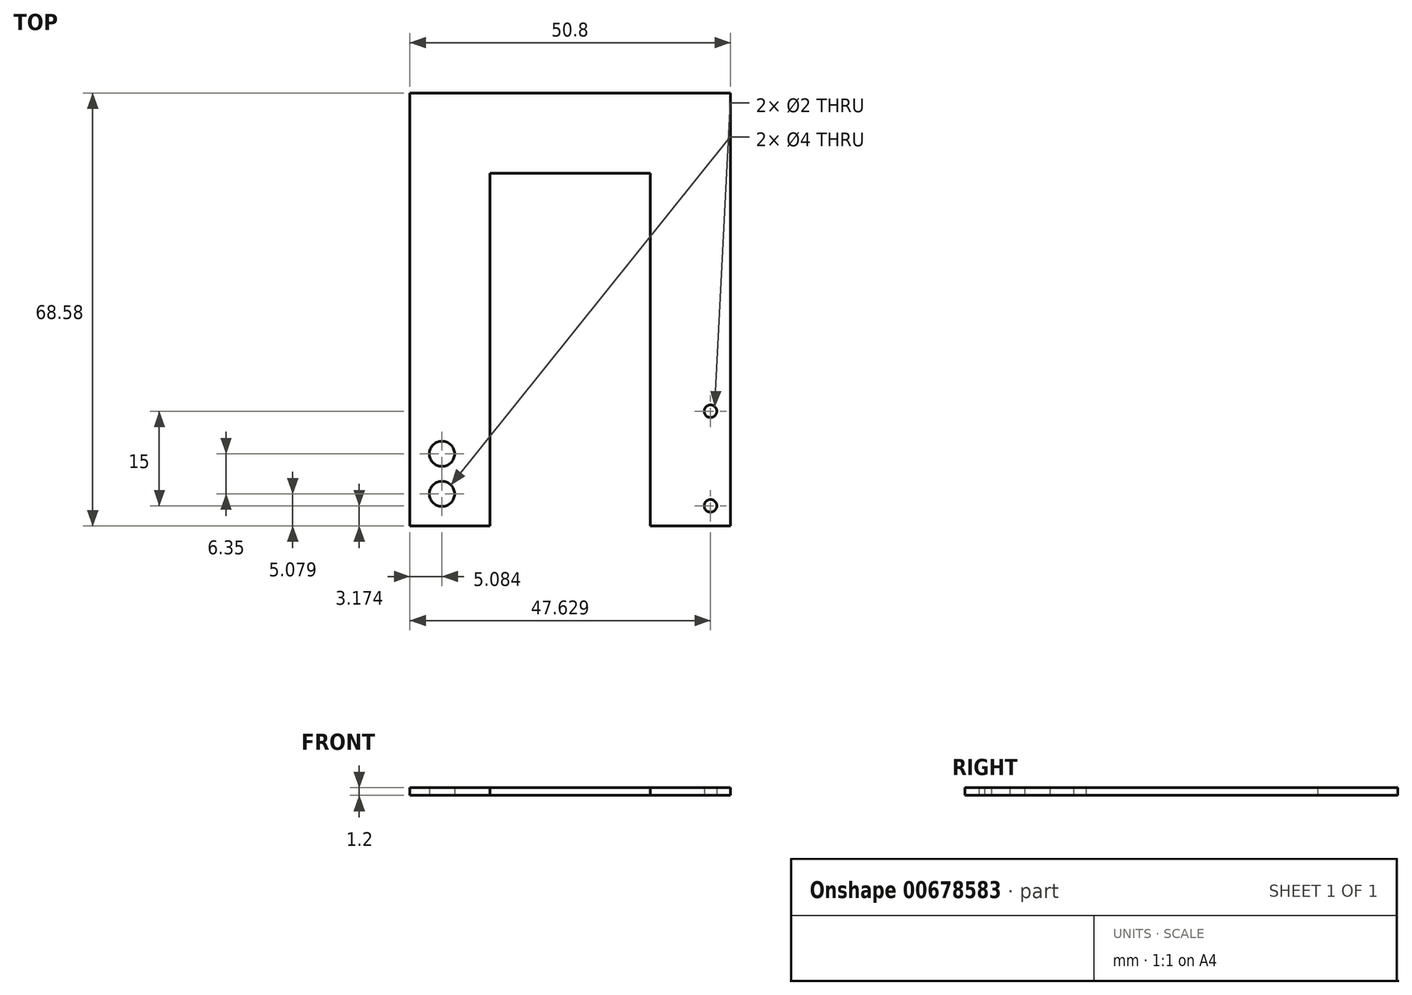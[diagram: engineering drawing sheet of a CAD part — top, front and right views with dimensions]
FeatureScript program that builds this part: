
annotation { "Feature Type Name" : "Feature", "Feature Type Description" : "" }
export const myFeature = defineFeature(function(context is Context, id is Id, definition is map)
    precondition{}
    {
        {
            var Q0;
            Q0=qCreatedBy(makeId("Top.planeOp"),FACE);
            var sketch = newSketch(context, id + "F0", { "sketchPlane" : qUnion([Q0])});
            skLineSegment(sketch, "E0.bottom", {"start": v(-54.64, 88.2) * mm, "end": v(-41.94, 88.2) * mm});
            skLineSegment(sketch, "E0.top", {"start": v(-54.64, 19.63) * mm, "end": v(-41.94, 19.63) * mm});
            skLineSegment(sketch, "E0.left", {"start": v(-54.64, 88.2) * mm, "end": v(-54.64, 19.63) * mm});
            skLineSegment(sketch, "E0.right", {"start": v(-41.94, 75.5) * mm, "end": v(-41.94, 19.63) * mm});
            skLineSegment(sketch, "E1.bottom", {"start": v(-41.94, 88.2) * mm, "end": v(-16.54, 88.2) * mm});
            skLineSegment(sketch, "E1.top", {"start": v(-41.94, 75.5) * mm, "end": v(-16.54, 75.5) * mm});
            skLineSegment(sketch, "E2.bottom", {"start": v(-16.54, 88.2) * mm, "end": v(-3.84, 88.2) * mm});
            skLineSegment(sketch, "E2.top", {"start": v(-16.54, 19.63) * mm, "end": v(-3.84, 19.63) * mm});
            skLineSegment(sketch, "E2.left", {"start": v(-16.54, 75.5) * mm, "end": v(-16.54, 19.63) * mm});
            skLineSegment(sketch, "E2.right", {"start": v(-3.84, 88.2) * mm, "end": v(-3.84, 19.63) * mm});
            skLineSegment(sketch, "E3", {"start": v(-29.24, 88.2) * mm, "end": v(-29.24, 75.5) * mm, "construction": true});
            skCircle(sketch, "E4", {"center": v(-7.01, 22.8) * mm, "radius": 1 * mm});
            skCircle(sketch, "E5", {"center": v(-7.01, 37.8) * mm, "radius": 1 * mm});
            skLineSegment(sketch, "E6", {"start": v(-7.01, 22.8) * mm, "end": v(-7.01, 37.8) * mm, "construction": true});
            skLineSegment(sketch, "E7", {"start": v(-7.01, 22.8) * mm, "end": v(-7.01, 19.63) * mm, "construction": true});
            skCircle(sketch, "E8", {"center": v(-49.56, 24.7) * mm, "radius": 2 * mm});
            skCircle(sketch, "E9", {"center": v(-49.56, 31.06) * mm, "radius": 2 * mm});
            skLineSegment(sketch, "E10", {"start": v(-49.56, 24.7) * mm, "end": v(-49.56, 31.06) * mm, "construction": true});
            skLineSegment(sketch, "E11", {"start": v(-49.56, 24.7) * mm, "end": v(-49.56, 19.63) * mm, "construction": true});
            skLineSegment(sketch, "E12", {"start": v(-7.01, 22.8) * mm, "end": v(-3.84, 22.8) * mm, "construction": true});
            skLineSegment(sketch, "E13", {"start": v(-49.56, 24.7) * mm, "end": v(-54.64, 24.7) * mm, "construction": true});
            skSolve(sketch);
        }
        {
            var Q0;
            Q0 = qSketchRegion(id + "F0", true);
            extrude(context, id + "F1", {"entities" : qUnion([Q0]), "depth" : 1.2 * mm, "offsetDistance" : 25.4 * mm});
        }
    });
